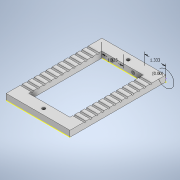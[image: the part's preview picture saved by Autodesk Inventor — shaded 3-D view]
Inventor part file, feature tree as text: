
AUTODESK INVENTOR PART (.ipt)
format: ipt  version: 2020 (Build 240168000, 168)  size: 199,168 bytes
history: native  units: in
note: dims shown in document units (in); Inventor stores cm internally (conversion verified against a paired STEP export)
features: sketch x5, hole x4, extrude x3
ambient origin geometry x8: Origin, YZ Plane, XZ Plane, XY Plane, X Axis, Y Axis, Z Axis, Center Point
bodies: Solid1 (feature_tree)
feature tree (12):
  extrude  "Extrusion1"  Depth=6.0in
  extrude  "Extrusion2"  Depth=0.375in
  extrude  "Extrusion3"  Depth=1.0in
  sketch  "Sketch4"  dims[d7=0.375in d8=0.0in d11=0.9375in]
  hole  "Hole1"  [1 undecoded]
  hole  "Hole2"  [1 undecoded]
  sketch  "Sketch7"  dims[d12=0.125in d13=4.7244in d15=0.375in d16=0.3937in d18=1.0in d20=4.25in d21=0.0in d22=1.333in d23=1.333in d24=0.0in d25=0.196in d26=0.5in d27=0.375in d28=0.25in d29=0.5635in d30=1.0in d31=0.0in d32=0.196in d33=0.5in d34=0.375in d35=0.25in d36=0.5635in d37=1.0in d38=0.0in d53=0.196in d54=0.75in d55=0.375in d56=0.25in d57=0.5635in d58=1.0in d59=0.0in d60=0.196in d61=0.75in d62=0.375in d63=0.25in d64=0.5635in d65=1.0in d66=0.0in]
  hole  "Hole5"  [1 undecoded]
  hole  "Hole6"  [1 undecoded]
  sketch  "Sketch1"  dims[d0=4.0in d1=6.0in]
  sketch  "Sketch2"  dims[d2=0.375in d3=0.0in d4=1.0in]
  sketch  "Sketch3"  dims[d5=135.0deg d6=1.0in]
note: 4 required parameter values undecoded (feature->parameter linkage not recoverable at this tier; creation-order binding heuristic only, values carry confidence <= 0.55)
